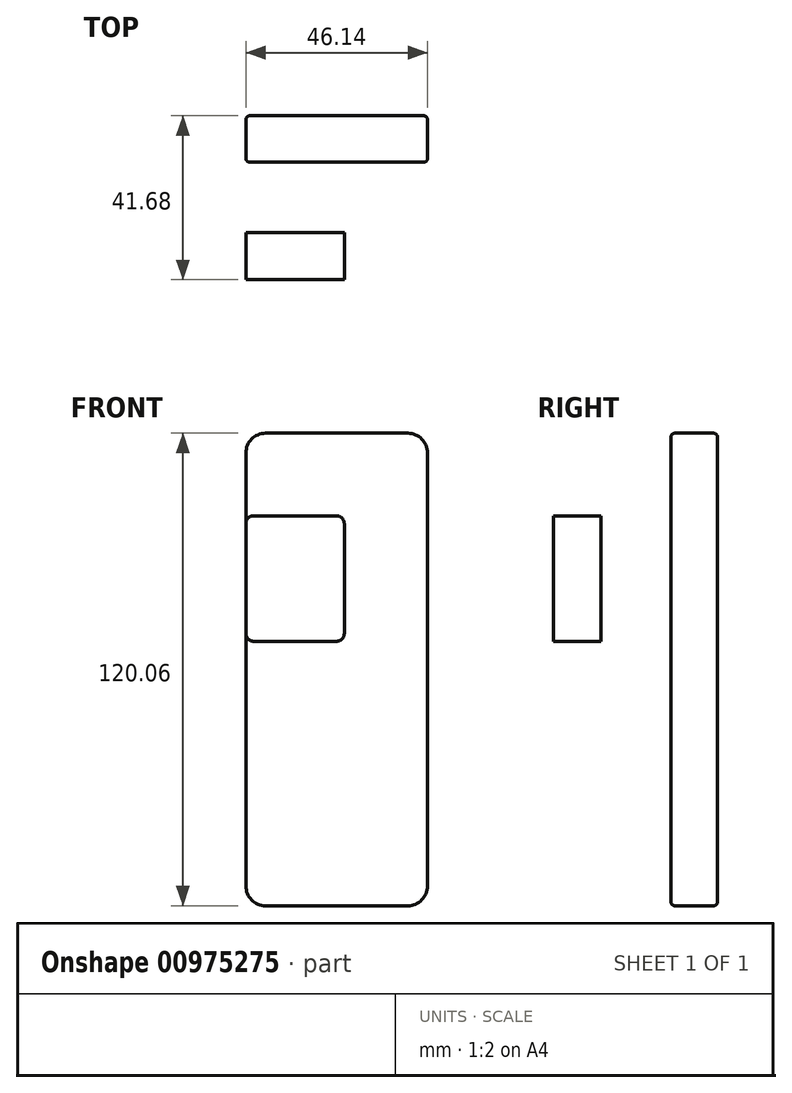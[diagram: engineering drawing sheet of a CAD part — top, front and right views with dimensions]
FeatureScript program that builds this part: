
annotation { "Feature Type Name" : "Feature", "Feature Type Description" : "" }
export const myFeature = defineFeature(function(context is Context, id is Id, definition is map)
    precondition{}
    {
        {
            var Q0;
            Q0=qCreatedBy(makeId("Right.planeOp"),FACE);
            var sketch = newSketch(context, id + "F0", { "sketchPlane" : qUnion([Q0])});
            skLineSegment(sketch, "E0.bottom", {"start": v(-11.83, 52.87) * mm, "end": v(0, 52.87) * mm});
            skLineSegment(sketch, "E0.top", {"start": v(-11.83, -67.19) * mm, "end": v(0, -67.19) * mm});
            skLineSegment(sketch, "E0.left", {"start": v(-11.83, 52.87) * mm, "end": v(-11.83, -67.19) * mm});
            skLineSegment(sketch, "E0.right", {"start": v(0, 52.87) * mm, "end": v(0, -67.19) * mm});
            skSolve(sketch);
        }
        {
            var Q0;
            Q0=qCreatedBy(makeId("Right.planeOp"),FACE);
            var sketch = newSketch(context, id + "F1", { "sketchPlane" : qUnion([Q0])});
            skLineSegment(sketch, "E1.bottom", {"start": v(-37.71, 31.9) * mm, "end": v(-29.68, 31.9) * mm});
            skLineSegment(sketch, "E1.top", {"start": v(-37.71, 0) * mm, "end": v(-29.68, 0) * mm});
            skLineSegment(sketch, "E1.left", {"start": v(-37.71, 31.9) * mm, "end": v(-37.71, 0) * mm});
            skLineSegment(sketch, "E1.right", {"start": v(-29.68, 31.9) * mm, "end": v(-29.68, 0) * mm});
            skSolve(sketch);
        }
        {
            var Q0;
            Q0=makeQuery(id+"F0.imprint","IMPRINT",FACE,{"disambiguationData":[TD([[makeQuery(id+"F0.imprint","IMPRINT",EDGE,{"derivedFrom":sQuery(id+"F0.wireOp",EDGE,"E0.bottom")}),-1.0]])]});
            var Q1;
            Q1 = qSketchRegion(id + "F0", true);
            extrude(context, id + "F2", {"entities" : qUnion([Q0, Q1]), "depth" : 46.14 * mm, "offsetDistance" : 25 * mm});
        }
        {
            var Q0;
            Q0=sQuery(id+"F1.wireOp",EDGE,"E1.right");
            extrude(context, id + "F3", {"bodyType" : ToolBodyType.SURFACE, "surfaceEntities" : qUnion([Q0]), "depth" : 25 * mm, "offsetDistance" : 25 * mm});
        }
        {
            var Q0;
            Q0=makeQuery(id+"F3.opExtrude","SWEPT_FACE",FACE,{"disambiguationData":[OSD([sQuery(id+"F1.wireOp",EDGE,"E1.right")])]});
            extrude(context, id + "F4", {"entities" : qUnion([Q0]), "depth" : 2 * mm, "offsetDistance" : 25 * mm});
        }
        {
            var Q0;
            Q0=makeQuery(id+"F2.opExtrude","CAP_EDGE",EDGE,{"disambiguationData":[OSD([sQuery(id+"F0.wireOp",EDGE,"E0.bottom")])],"isStart":false});
            var Q1;
            Q1=makeQuery(id+"F2.opExtrude","CAP_EDGE",EDGE,{"disambiguationData":[OSD([sQuery(id+"F0.wireOp",EDGE,"E0.bottom")])],"isStart":true});
            var Q2;
            Q2=makeQuery(id+"F2.opExtrude","CAP_EDGE",EDGE,{"disambiguationData":[OSD([sQuery(id+"F0.wireOp",EDGE,"E0.top")])],"isStart":false});
            var Q3;
            Q3=makeQuery(id+"F2.opExtrude","CAP_EDGE",EDGE,{"disambiguationData":[OSD([sQuery(id+"F0.wireOp",EDGE,"E0.top")])],"isStart":true});
            fillet(context, id + "F5", {"entities" : qUnion([Q0, Q1, Q2, Q3]), "radius" : 5 * mm, "tangentPropagation" : true, "allowEdgeOverflow" : false});
        }
        {
            var Q0;
            Q0=makeQuery(id+"F2.opExtrude","CAP_EDGE",EDGE,{"disambiguationData":[OSD([sQuery(id+"F0.wireOp",EDGE,"E0.right")])],"isStart":false});
            var Q1;
            Q1=makeQuery(id+"F2.opExtrude","CAP_EDGE",EDGE,{"disambiguationData":[OSD([sQuery(id+"F0.wireOp",EDGE,"E0.left")])],"isStart":true});
            fillet(context, id + "F6", {"entities" : qUnion([Q0, Q1]), "radius" : 1 * mm, "tangentPropagation" : true, "allowEdgeOverflow" : false});
        }
        {
            var Q0;
            {var subQ0=sQuery(id+"F1.wireOp",VERTEX,"E1.right.start");Q0=makeQuery(id+"F4.opExtrude","SWEPT_EDGE",EDGE,{"disambiguationData":[OSD([subQ0]),TDD([makeQuery(id+"F3.opExtrude","CAP_VERTEX",VERTEX,{"disambiguationData":[OSD([subQ0])],"isStart":true})])]});}
            var Q1;
            {var subQ0=sQuery(id+"F1.wireOp",VERTEX,"E1.right.start");Q1=makeQuery(id+"F4.opExtrude","SWEPT_EDGE",EDGE,{"disambiguationData":[OSD([subQ0]),TDD([makeQuery(id+"F3.opExtrude","CAP_VERTEX",VERTEX,{"disambiguationData":[OSD([subQ0])],"isStart":false})])]});}
            var Q2;
            {var subQ0=sQuery(id+"F1.wireOp",VERTEX,"E1.right.end");Q2=makeQuery(id+"F4.opExtrude","SWEPT_EDGE",EDGE,{"disambiguationData":[OSD([subQ0]),TDD([makeQuery(id+"F3.opExtrude","CAP_VERTEX",VERTEX,{"disambiguationData":[OSD([subQ0])],"isStart":false})])]});}
            var Q3;
            {var subQ0=sQuery(id+"F1.wireOp",VERTEX,"E1.right.end");Q3=makeQuery(id+"F4.opExtrude","SWEPT_EDGE",EDGE,{"disambiguationData":[OSD([subQ0]),TDD([makeQuery(id+"F3.opExtrude","CAP_VERTEX",VERTEX,{"disambiguationData":[OSD([subQ0])],"isStart":true})])]});}
            fillet(context, id + "F7", {"entities" : qUnion([Q0, Q1, Q2, Q3]), "radius" : 2 * mm, "tangentPropagation" : true, "allowEdgeOverflow" : false});
        }
        {
            var Q0;
            Q0=makeQuery(id+"F4.opExtrude","CAP_FACE",FACE,{"disambiguationData":[OSD([sQuery(id+"F1.wireOp",EDGE,"E1.right")])],"isStart":false});
            extrude(context, id + "F8", {"entities" : qUnion([Q0]), "operationType" : NewBodyOperationType.ADD, "depth" : 10 * mm, "offsetDistance" : 25 * mm});
        }
    });
